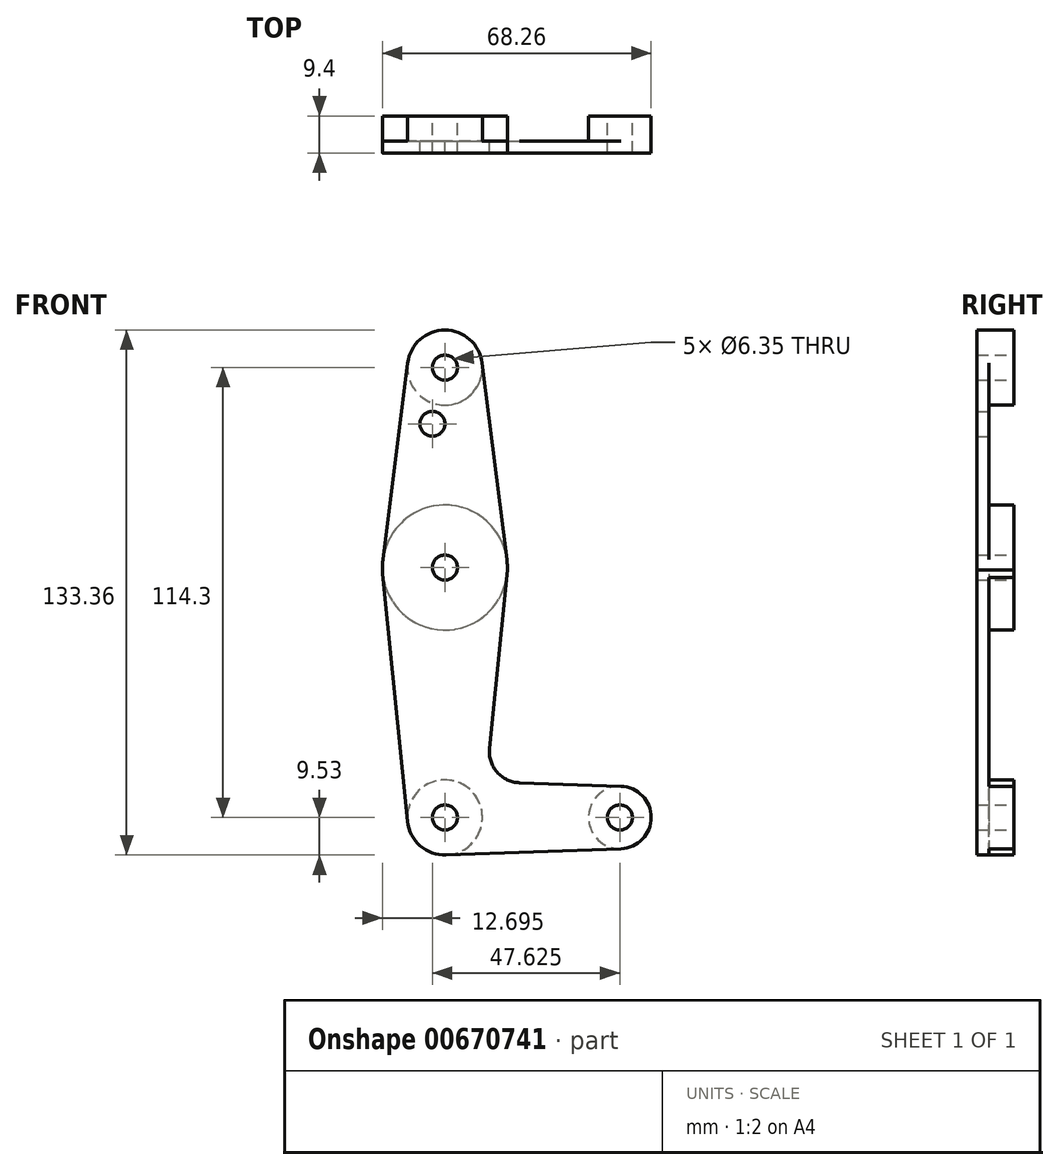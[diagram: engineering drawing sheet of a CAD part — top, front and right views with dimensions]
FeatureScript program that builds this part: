
annotation { "Feature Type Name" : "Feature", "Feature Type Description" : "" }
export const myFeature = defineFeature(function(context is Context, id is Id, definition is map)
    precondition{}
    {
        {
            var Q0;
            Q0=qCreatedBy(makeId("Front.planeOp"),FACE);
            var sketch = newSketch(context, id + "F0", { "sketchPlane" : qUnion([Q0])});
            skCircle(sketch, "E0", {"center": v(0, 0) * mm, "radius": 9.53 * mm});
            skLineSegment(sketch, "E1", {"start": v(0, 0) * mm, "end": v(0, 114.3) * mm, "construction": true});
            skLineSegment(sketch, "E2", {"start": v(0, 0) * mm, "end": v(44.45, 0) * mm, "construction": true});
            skCircle(sketch, "E3", {"center": v(0, 114.3) * mm, "radius": 9.53 * mm});
            skCircle(sketch, "E4", {"center": v(0, 63.5) * mm, "radius": 15.88 * mm});
            skCircle(sketch, "E5", {"center": v(44.45, 0) * mm, "radius": 7.94 * mm});
            skLineSegment(sketch, "E6", {"start": v(-15.75, 65.48) * mm, "end": v(-9.45, 115.5) * mm});
            skLineSegment(sketch, "E7", {"start": v(9.45, 115.5) * mm, "end": v(15.75, 65.48) * mm});
            skLineSegment(sketch, "E8", {"start": v(0.34, -9.52) * mm, "end": v(44.73, -7.93) * mm});
            skCircle(sketch, "E9", {"center": v(0, 114.3) * mm, "radius": 3.18 * mm});
            skCircle(sketch, "E10", {"center": v(0, 63.5) * mm, "radius": 3.18 * mm});
            skCircle(sketch, "E11", {"center": v(0, 0) * mm, "radius": 3.18 * mm});
            skCircle(sketch, "E12", {"center": v(44.45, 0) * mm, "radius": 3.18 * mm});
            skCircle(sketch, "E13", {"center": v(-3.18, 100.03) * mm, "radius": 3.18 * mm});
            skLineSegment(sketch, "E14", {"start": v(-15.8, 61.91) * mm, "end": v(-9.48, -0.95) * mm});
            skLineSegment(sketch, "E15", {"start": v(15.86, 62.85) * mm, "end": v(11.33, 17.55) * mm});
            skLineSegment(sketch, "E16", {"start": v(18.97, 8.81) * mm, "end": v(44.72, 7.93) * mm});
            skArc(sketch, "E17.filletArc", {"start": v(11.33, 17.55) * mm, "mid": v(13.25, 11.53) * mm, "end": v(18.97, 8.81) * mm});
            skSolve(sketch);
        }
        {
            var Q0;
            {var subQ1=sQuery(id+"F0.wireOp",EDGE,"E6");Q0=makeQuery(id+"F0.imprint","IMPRINT",FACE,{"disambiguationData":[TD([[makeQuery(id+"F0.imprint","IMPRINT",EDGE,{"derivedFrom":subQ1}),-1.0]])]});}
            var Q1;
            {var subQ0=sQuery(id+"F0.wireOp",EDGE,"E8");Q1=makeQuery(id+"F0.imprint","IMPRINT",FACE,{"disambiguationData":[TD([[makeQuery(id+"F0.imprint","IMPRINT",EDGE,{"derivedFrom":subQ0}),1.0]])]});}
            var Q2;
            Q2=makeQuery(id+"F0.imprint","IMPRINT",FACE,{"disambiguationData":[TD([[makeQuery(id+"F0.imprint","IMPRINT",EDGE,{"derivedFrom":sQuery(id+"F0.wireOp",EDGE,"E9")}),-1.0]])]});
            var Q3;
            Q3=makeQuery(id+"F0.imprint","IMPRINT",FACE,{"disambiguationData":[TD([[makeQuery(id+"F0.imprint","IMPRINT",EDGE,{"derivedFrom":sQuery(id+"F0.wireOp",EDGE,"E10")}),-1.0]])]});
            var Q4;
            Q4=makeQuery(id+"F0.imprint","IMPRINT",FACE,{"disambiguationData":[TD([[makeQuery(id+"F0.imprint","IMPRINT",EDGE,{"derivedFrom":sQuery(id+"F0.wireOp",EDGE,"E11")}),-1.0]])]});
            var Q5;
            Q5=makeQuery(id+"F0.imprint","IMPRINT",FACE,{"disambiguationData":[TD([[makeQuery(id+"F0.imprint","IMPRINT",EDGE,{"derivedFrom":sQuery(id+"F0.wireOp",EDGE,"E12")}),-1.0]])]});
            extrude(context, id + "F1", {"entities" : qUnion([Q0, Q1, Q2, Q3, Q4, Q5]), "depth" : 3.05 * mm, "offsetDistance" : 25.4 * mm});
        }
        {
            var Q0;
            Q0=makeQuery(id+"F0.imprint","IMPRINT",FACE,{"disambiguationData":[TD([[makeQuery(id+"F0.imprint","IMPRINT",EDGE,{"derivedFrom":sQuery(id+"F0.wireOp",EDGE,"E12")}),-1.0]])]});
            var Q1;
            Q1=makeQuery(id+"F0.imprint","IMPRINT",FACE,{"disambiguationData":[TD([[makeQuery(id+"F0.imprint","IMPRINT",EDGE,{"derivedFrom":sQuery(id+"F0.wireOp",EDGE,"E11")}),-1.0]])]});
            var Q2;
            Q2=makeQuery(id+"F0.imprint","IMPRINT",FACE,{"disambiguationData":[TD([[makeQuery(id+"F0.imprint","IMPRINT",EDGE,{"derivedFrom":sQuery(id+"F0.wireOp",EDGE,"E10")}),-1.0]])]});
            var Q3;
            Q3=makeQuery(id+"F0.imprint","IMPRINT",FACE,{"disambiguationData":[TD([[makeQuery(id+"F0.imprint","IMPRINT",EDGE,{"derivedFrom":sQuery(id+"F0.wireOp",EDGE,"E9")}),-1.0]])]});
            extrude(context, id + "F2", {"entities" : qUnion([Q0, Q1, Q2, Q3]), "operationType" : NewBodyOperationType.ADD, "oppositeDirection" : true, "depth" : 6.35 * mm, "offsetDistance" : 25.4 * mm});
        }
    });
